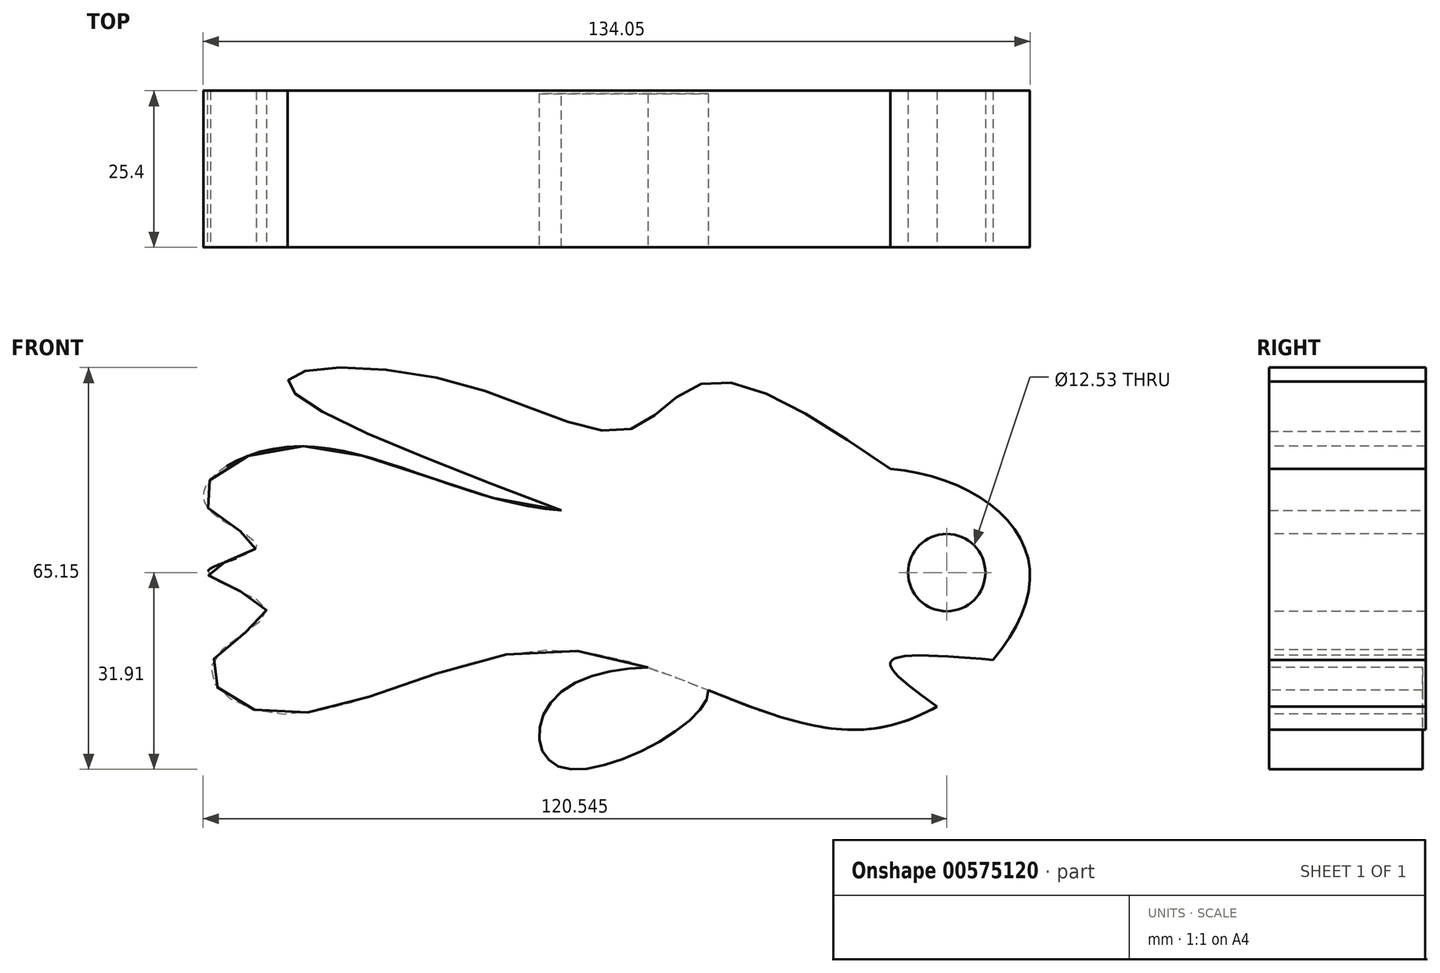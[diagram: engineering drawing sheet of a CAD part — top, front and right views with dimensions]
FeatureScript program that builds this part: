
annotation { "Feature Type Name" : "Feature", "Feature Type Description" : "" }
export const myFeature = defineFeature(function(context is Context, id is Id, definition is map)
    precondition{}
    {
        {
            var Q0;
            Q0=qCreatedBy(makeId("Front.planeOp"),FACE);
            var sketch = newSketch(context, id + "F0", { "sketchPlane" : qUnion([Q0])});
            skFitSpline(sketch, "E0", {"points": [v(-46.3, -22.87) * mm, v(0, -12.54) * mm, v(50.95, -25.25) * mm, v(75.96, 0) * mm, v(53.33, 16.83) * mm, v(0, 10.08) * mm, v(-44.32, 20.4) * mm, v(-57.82, 11.27) * mm, v(-49.48, 4.13) * mm, v(-57.42, 0) * mm, v(-47.9, -5.8) * mm, v(-56.63, -14.53) * mm, v(-46.3, -22.87) * mm]});
            skFitSpline(sketch, "E1", {"points": [v(53.33, 16.83) * mm, v(23.16, 30.73) * mm, v(10.86, 23.18) * mm, v(-18.12, 31.12) * mm, v(-44.32, 31.12) * mm, v(0, 10.08) * mm], "startDerivative": vector(-162.05, 110.12) * mm, "endDerivative": vector(265, -100.51) * mm});
            skSolve(sketch);
        }
        {
            var Q0;
            {var subQ0=sQuery(id+"F0.wireOp",EDGE,"E1");var subQ1=sQuery(id+"F0.wireOp",EDGE,"E0");var subQ2=makeQuery(id+"F0.imprint","INTERSECT",VERTEX,{"disambiguationData":[OD(0.0)],"derivedFrom":[subQ1,subQ0]});Q0=makeQuery(id+"F0.imprint","IMPRINT",FACE,{"disambiguationData":[TD([[makeQuery(id+"F0.imprint","IMPRINT",EDGE,{"disambiguationData":[TD([[subQ2,-1.0]])],"derivedFrom":subQ1}),1.0]])]});}
            var Q1;
            {var subQ0=sQuery(id+"F0.wireOp",EDGE,"E1");Q1=makeQuery(id+"F0.imprint","IMPRINT",FACE,{"disambiguationData":[TD([[makeQuery(id+"F0.imprint","IMPRINT",EDGE,{"derivedFrom":subQ0}),1.0]])]});}
            extrude(context, id + "F1", {"entities" : qUnion([Q0, Q1]), "depth" : 25.4 * mm, "offsetDistance" : 25.4 * mm});
        }
        {
            var Q0;
            Q0=makeQuery(id+"F1.opExtrude","CAP_FACE",FACE,{"disambiguationData":[OSD([sQuery(id+"F0.wireOp",EDGE,"E0"),sQuery(id+"F0.wireOp",EDGE,"E1")])],"isStart":false});
            var sketch = newSketch(context, id + "F2", { "sketchPlane" : qUnion([Q0])});
            skCircle(sketch, "E2", {"center": v(62.46, 0) * mm, "radius": 6.27 * mm});
            skFitSpline(sketch, "E3", {"points": [v(69.98, -14.16) * mm, v(53.33, -14.53) * mm, v(60.9, -21.7) * mm], "startDerivative": vector(-42.92, 3.69) * mm, "endDerivative": vector(27.55, -19.78) * mm});
            skSolve(sketch);
        }
        {
            var Q0;
            {var subQ0=sQuery(id+"F2.wireOp",EDGE,"E3");Q0=makeQuery(id+"F2.imprint","IMPRINT",FACE,{"disambiguationData":[TD([[makeQuery(id+"F2.imprint","IMPRINT",EDGE,{"derivedFrom":subQ0}),1.0]])]});}
            var Q1;
            Q1=makeQuery(id+"F2.imprint","IMPRINT",FACE,{"disambiguationData":[TD([[makeQuery(id+"F2.imprint","IMPRINT",EDGE,{"derivedFrom":sQuery(id+"F2.wireOp",EDGE,"E2")}),1.0]])]});
            extrude(context, id + "F3", {"entities" : qUnion([Q0, Q1]), "operationType" : NewBodyOperationType.REMOVE, "oppositeDirection" : true, "depth" : 25.4 * mm, "offsetDistance" : 25.4 * mm});
        }
        {
            var Q0;
            Q0=makeQuery(id+"F1.opExtrude","CAP_FACE",FACE,{"disambiguationData":[OSD([sQuery(id+"F0.wireOp",EDGE,"E0"),sQuery(id+"F0.wireOp",EDGE,"E1")])],"isStart":false});
            var sketch = newSketch(context, id + "F4", { "sketchPlane" : qUnion([Q0])});
            skFitSpline(sketch, "E4", {"points": [v(23.8, -19.06) * mm, v(0, -31.6) * mm, v(0, -19.3) * mm, v(23.8, -19.06) * mm]});
            skSolve(sketch);
        }
        {
            var Q0;
            {var subQ0=sQuery(id+"F4.wireOp",EDGE,"E4");var subQ1=makeQuery(id+"F3.boolean.opBoolean","SPLIT",EDGE,{"disambiguationData":[OD(1.0)],"derivedFrom":makeQuery(id+"F1.opExtrude","CAP_EDGE",EDGE,{"disambiguationData":[OSD([sQuery(id+"F0.wireOp",EDGE,"E0")])],"isStart":false})});var subQ2=makeQuery(id+"F4.imprint","INTERSECT",VERTEX,{"disambiguationData":[OD(0.0)],"derivedFrom":[subQ1,subQ0]});Q0=makeQuery(id+"F4.imprint","IMPRINT",FACE,{"disambiguationData":[TD([[makeQuery(id+"F4.imprint","IMPRINT",EDGE,{"disambiguationData":[TD([[subQ2,1.0]])],"derivedFrom":subQ0}),-1.0]])]});}
            extrude(context, id + "F5", {"entities" : qUnion([Q0]), "operationType" : NewBodyOperationType.ADD, "oppositeDirection" : true, "depth" : 24.9 * mm, "offsetDistance" : 25.4 * mm});
        }
    });
